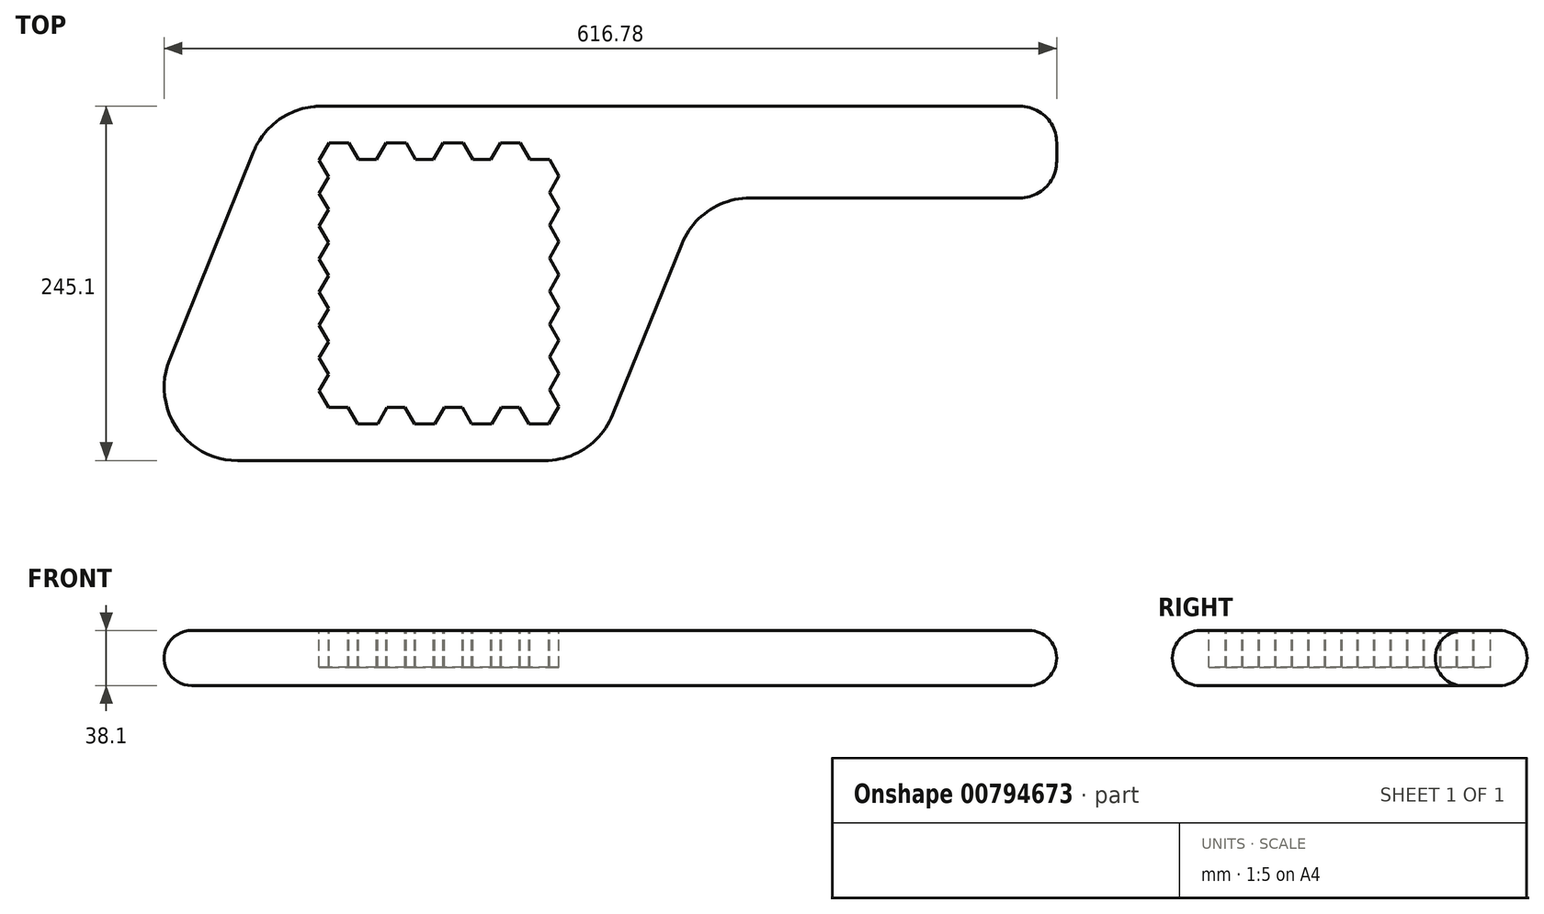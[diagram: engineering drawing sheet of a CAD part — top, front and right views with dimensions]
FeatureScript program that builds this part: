
annotation { "Feature Type Name" : "Feature", "Feature Type Description" : "" }
export const myFeature = defineFeature(function(context is Context, id is Id, definition is map)
    precondition{}
    {
        {
            var Q0;
            Q0=qCreatedBy(makeId("Top.planeOp"),FACE);
            var sketch = newSketch(context, id + "F0", { "sketchPlane" : qUnion([Q0])});
            skLineSegment(sketch, "E0", {"start": v(-82.07, 74.66) * mm, "end": v(-88.65, 63.27) * mm});
            skLineSegment(sketch, "E1", {"start": v(-88.65, 63.27) * mm, "end": v(-82.07, 51.88) * mm});
            skLineSegment(sketch, "E2", {"start": v(-82.07, 51.88) * mm, "end": v(-88.65, 40.49) * mm});
            skLineSegment(sketch, "E3", {"start": v(-88.65, 40.49) * mm, "end": v(-82.07, 29.1) * mm});
            skLineSegment(sketch, "E4", {"start": v(-82.07, 29.1) * mm, "end": v(-88.65, 17.7) * mm});
            skLineSegment(sketch, "E5", {"start": v(-88.65, 17.7) * mm, "end": v(-82.07, 6.31) * mm});
            skLineSegment(sketch, "E6", {"start": v(-82.07, 6.31) * mm, "end": v(-88.65, -5.08) * mm});
            skLineSegment(sketch, "E7", {"start": v(-88.65, -5.08) * mm, "end": v(-82.07, -16.47) * mm});
            skLineSegment(sketch, "E8", {"start": v(-82.07, -16.47) * mm, "end": v(-88.65, -27.86) * mm});
            skLineSegment(sketch, "E9", {"start": v(-88.65, -27.86) * mm, "end": v(-82.07, -39.26) * mm});
            skLineSegment(sketch, "E10", {"start": v(-82.07, -39.26) * mm, "end": v(-88.65, -50.65) * mm});
            skLineSegment(sketch, "E11", {"start": v(-88.65, -50.65) * mm, "end": v(-82.07, -62.04) * mm});
            skLineSegment(sketch, "E12", {"start": v(-82.07, -62.04) * mm, "end": v(-88.65, -73.43) * mm});
            skLineSegment(sketch, "E13", {"start": v(-88.65, -73.43) * mm, "end": v(-82.07, -84.82) * mm});
            skLineSegment(sketch, "E14", {"start": v(-82.07, -84.82) * mm, "end": v(-68.55, -84.81) * mm});
            skLineSegment(sketch, "E15", {"start": v(-68.55, -84.81) * mm, "end": v(-61.98, -96.2) * mm});
            skLineSegment(sketch, "E16", {"start": v(-61.98, -96.2) * mm, "end": v(-48.07, -96.2) * mm});
            skLineSegment(sketch, "E17", {"start": v(-48.07, -96.2) * mm, "end": v(-41.5, -84.81) * mm});
            skLineSegment(sketch, "E18", {"start": v(-41.5, -84.81) * mm, "end": v(-29.1, -84.81) * mm});
            skLineSegment(sketch, "E19", {"start": v(-29.1, -84.81) * mm, "end": v(-22.51, -96.2) * mm});
            skLineSegment(sketch, "E20", {"start": v(-22.51, -96.2) * mm, "end": v(-8.61, -96.2) * mm});
            skLineSegment(sketch, "E21", {"start": v(-8.61, -96.2) * mm, "end": v(-2.03, -84.81) * mm});
            skLineSegment(sketch, "E22", {"start": v(-2.03, -84.81) * mm, "end": v(10.37, -84.81) * mm});
            skLineSegment(sketch, "E23", {"start": v(10.37, -84.81) * mm, "end": v(16.95, -96.2) * mm});
            skLineSegment(sketch, "E24", {"start": v(16.95, -96.2) * mm, "end": v(30.85, -96.2) * mm});
            skLineSegment(sketch, "E25", {"start": v(30.85, -96.2) * mm, "end": v(37.43, -84.81) * mm});
            skLineSegment(sketch, "E26", {"start": v(37.43, -84.81) * mm, "end": v(49.84, -84.81) * mm});
            skLineSegment(sketch, "E27", {"start": v(49.84, -84.81) * mm, "end": v(56.41, -96.2) * mm});
            skLineSegment(sketch, "E28", {"start": v(56.41, -96.2) * mm, "end": v(70.3, -96.2) * mm});
            skLineSegment(sketch, "E29", {"start": v(70.3, -96.2) * mm, "end": v(77.26, -84.16) * mm});
            skLineSegment(sketch, "E30", {"start": v(77.26, -84.16) * mm, "end": v(70.68, -72.77) * mm});
            skLineSegment(sketch, "E31", {"start": v(70.68, -72.77) * mm, "end": v(77.26, -61.38) * mm});
            skLineSegment(sketch, "E32", {"start": v(77.26, -61.38) * mm, "end": v(70.68, -49.99) * mm});
            skLineSegment(sketch, "E33", {"start": v(70.68, -49.99) * mm, "end": v(77.26, -38.6) * mm});
            skLineSegment(sketch, "E34", {"start": v(77.26, -38.6) * mm, "end": v(70.68, -27.2) * mm});
            skLineSegment(sketch, "E35", {"start": v(70.68, -27.2) * mm, "end": v(77.26, -15.81) * mm});
            skLineSegment(sketch, "E36", {"start": v(77.26, -15.81) * mm, "end": v(70.68, -4.42) * mm});
            skLineSegment(sketch, "E37", {"start": v(70.68, -4.42) * mm, "end": v(77.26, 6.97) * mm});
            skLineSegment(sketch, "E38", {"start": v(77.26, 6.97) * mm, "end": v(70.68, 18.36) * mm});
            skLineSegment(sketch, "E39", {"start": v(70.68, 18.36) * mm, "end": v(77.26, 29.76) * mm});
            skLineSegment(sketch, "E40", {"start": v(77.26, 29.76) * mm, "end": v(70.68, 41.15) * mm});
            skLineSegment(sketch, "E41", {"start": v(70.68, 41.15) * mm, "end": v(77.26, 52.54) * mm});
            skLineSegment(sketch, "E42", {"start": v(77.26, 52.54) * mm, "end": v(70.68, 63.93) * mm});
            skLineSegment(sketch, "E43", {"start": v(70.68, 63.93) * mm, "end": v(77.26, 75.32) * mm});
            skLineSegment(sketch, "E44", {"start": v(77.26, 75.32) * mm, "end": v(70.68, 86.72) * mm});
            skLineSegment(sketch, "E45", {"start": v(70.68, 86.72) * mm, "end": v(57.16, 86.7) * mm});
            skLineSegment(sketch, "E46", {"start": v(57.16, 86.7) * mm, "end": v(50.59, 98.1) * mm});
            skLineSegment(sketch, "E47", {"start": v(50.59, 98.1) * mm, "end": v(36.68, 98.1) * mm});
            skLineSegment(sketch, "E48", {"start": v(36.68, 98.1) * mm, "end": v(30.1, 86.7) * mm});
            skLineSegment(sketch, "E49", {"start": v(30.1, 86.7) * mm, "end": v(17.7, 86.7) * mm});
            skLineSegment(sketch, "E50", {"start": v(17.7, 86.7) * mm, "end": v(11.12, 98.1) * mm});
            skLineSegment(sketch, "E51", {"start": v(11.12, 98.1) * mm, "end": v(-2.78, 98.1) * mm});
            skLineSegment(sketch, "E52", {"start": v(-2.78, 98.1) * mm, "end": v(-9.36, 86.7) * mm});
            skLineSegment(sketch, "E53", {"start": v(-9.36, 86.7) * mm, "end": v(-21.77, 86.7) * mm});
            skLineSegment(sketch, "E54", {"start": v(-21.77, 86.7) * mm, "end": v(-28.34, 98.1) * mm});
            skLineSegment(sketch, "E55", {"start": v(-28.34, 98.1) * mm, "end": v(-42.25, 98.1) * mm});
            skLineSegment(sketch, "E56", {"start": v(-42.25, 98.1) * mm, "end": v(-48.83, 86.7) * mm});
            skLineSegment(sketch, "E57", {"start": v(-48.83, 86.7) * mm, "end": v(-61.24, 86.7) * mm});
            skLineSegment(sketch, "E58", {"start": v(-61.24, 86.7) * mm, "end": v(-67.81, 98.1) * mm});
            skLineSegment(sketch, "E59", {"start": v(-67.81, 98.1) * mm, "end": v(-81.7, 98.1) * mm});
            skLineSegment(sketch, "E60", {"start": v(-81.7, 98.1) * mm, "end": v(-88.65, 86.06) * mm});
            skLineSegment(sketch, "E61", {"start": v(-88.65, 86.06) * mm, "end": v(-82.07, 74.66) * mm});
            skSolve(sketch);
        }
        {
            var Q0;
            Q0=qCreatedBy(makeId("Top.planeOp"),FACE);
            var sketch = newSketch(context, id + "F1", { "sketchPlane" : qUnion([Q0])});
            skLineSegment(sketch, "E62.bottom", {"start": v(-86.81, 123.5) * mm, "end": v(101.62, 123.5) * mm});
            skLineSegment(sketch, "E62.top", {"start": v(-121.55, -121.6) * mm, "end": v(67.35, -121.6) * mm});
            skLineSegment(sketch, "E63", {"start": v(-121.55, -121.6) * mm, "end": v(-144.79, -121.6) * mm});
            skLineSegment(sketch, "E64", {"start": v(-191.89, -51.77) * mm, "end": v(-133.91, 91.73) * mm});
            skPoint(sketch, "E65.visualSharp", {"position": v(-121.08, 123.5) * mm});
            skArc(sketch, "E65.filletArc", {"start": v(-86.81, 123.5) * mm, "mid": v(-115.22, 114.81) * mm, "end": v(-133.91, 91.73) * mm});
            skPoint(sketch, "E66.visualSharp", {"position": v(-220.1, -121.6) * mm});
            skArc(sketch, "E66.filletArc", {"start": v(-191.89, -51.77) * mm, "mid": v(-186.9, -99.2) * mm, "end": v(-144.79, -121.6) * mm});
            skLineSegment(sketch, "E67", {"start": v(114.45, -89.83) * mm, "end": v(162.15, 28.23) * mm});
            skLineSegment(sketch, "E68.bottom", {"start": v(101.62, 123.5) * mm, "end": v(395.79, 123.5) * mm});
            skLineSegment(sketch, "E68.top", {"start": v(209.25, 60) * mm, "end": v(395.79, 60) * mm});
            skLineSegment(sketch, "E68.right", {"start": v(421.19, 98.1) * mm, "end": v(421.19, 85.4) * mm});
            skPoint(sketch, "E69.visualSharp", {"position": v(101.62, -121.6) * mm});
            skArc(sketch, "E69.filletArc", {"start": v(67.35, -121.6) * mm, "mid": v(95.76, -112.92) * mm, "end": v(114.45, -89.83) * mm});
            skPoint(sketch, "E70.visualSharp", {"position": v(174.99, 60) * mm});
            skArc(sketch, "E70.filletArc", {"start": v(209.25, 60) * mm, "mid": v(180.84, 51.31) * mm, "end": v(162.15, 28.23) * mm});
            skPoint(sketch, "E71.visualSharp", {"position": v(421.19, 60) * mm});
            skArc(sketch, "E71.filletArc", {"start": v(395.79, 60) * mm, "mid": v(413.75, 67.43) * mm, "end": v(421.19, 85.4) * mm});
            skPoint(sketch, "E72.visualSharp", {"position": v(421.19, 123.5) * mm});
            skArc(sketch, "E72.filletArc", {"start": v(421.19, 98.1) * mm, "mid": v(413.75, 116.06) * mm, "end": v(395.79, 123.5) * mm});
            skSolve(sketch);
        }
        {
            var Q0;
            Q0 = qSketchRegion(id + "F1", true);
            extrude(context, id + "F2", {"entities" : qUnion([Q0]), "oppositeDirection" : true, "depth" : 38.1 * mm, "offsetDistance" : 25.4 * mm});
        }
        {
            var Q0;
            Q0 = qSketchRegion(id + "F0", true);
            extrude(context, id + "F3", {"entities" : qUnion([Q0]), "operationType" : NewBodyOperationType.REMOVE, "oppositeDirection" : true, "depth" : 25.4 * mm, "offsetDistance" : 25.4 * mm});
        }
        {
            var Q0;
            Q0=makeQuery(id+"F2.opExtrude","CAP_EDGE",EDGE,{"disambiguationData":[OSD([sQuery(id+"F1.wireOp",EDGE,"E62.bottom"),sQuery(id+"F1.wireOp",EDGE,"E68.bottom")])],"isStart":true});
            fillet(context, id + "F4", {"entities" : qUnion([Q0]), "radius" : 19.05 * mm, "tangentPropagation" : true, "allowEdgeOverflow" : false});
        }
        {
            var Q0;
            Q0=makeQuery(id+"F2.opExtrude","CAP_EDGE",EDGE,{"disambiguationData":[OSD([sQuery(id+"F1.wireOp",EDGE,"E62.top"),sQuery(id+"F1.wireOp",EDGE,"E63")])],"isStart":false});
            fillet(context, id + "F5", {"entities" : qUnion([Q0]), "radius" : 19.05 * mm, "tangentPropagation" : true, "allowEdgeOverflow" : false});
        }
    });
